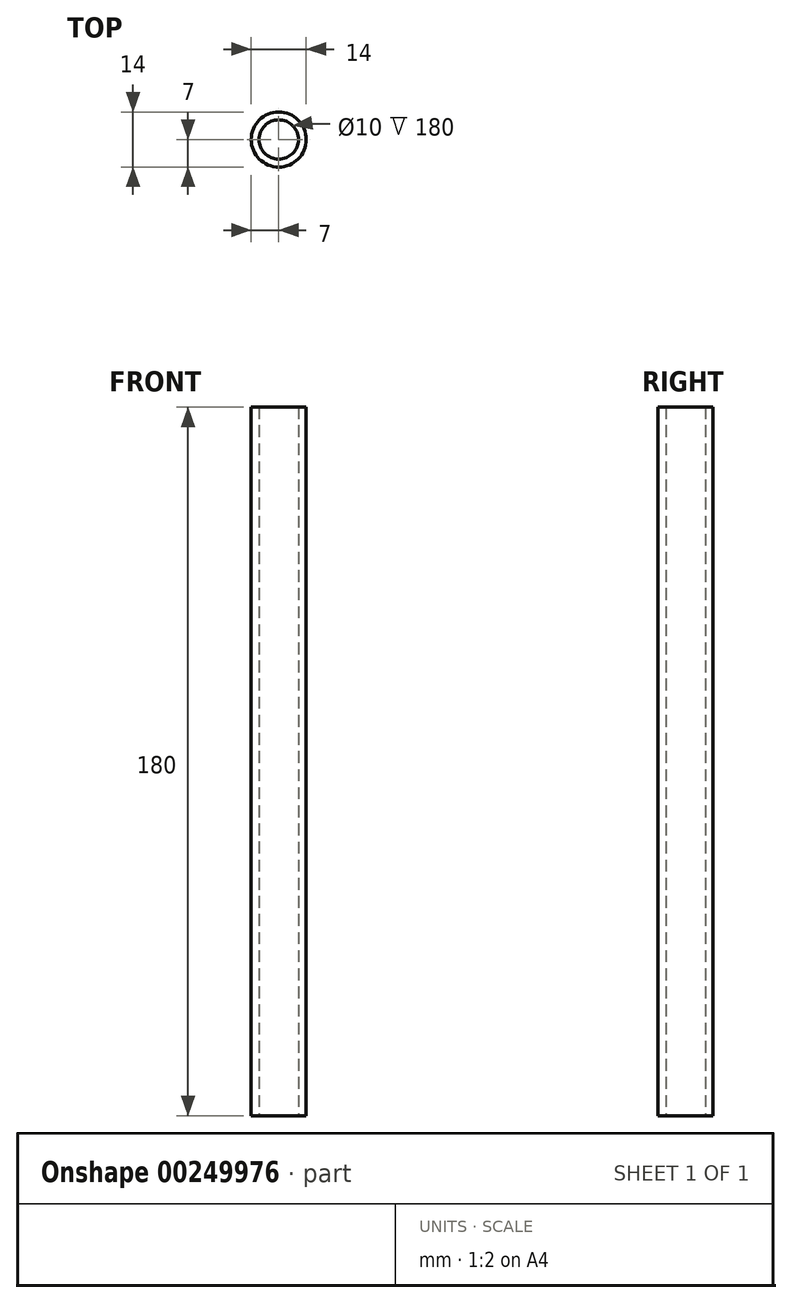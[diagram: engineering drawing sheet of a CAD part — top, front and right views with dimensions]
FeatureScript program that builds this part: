
annotation { "Feature Type Name" : "Feature", "Feature Type Description" : "" }
export const myFeature = defineFeature(function(context is Context, id is Id, definition is map)
    precondition{}
    {
        {
            var Q0;
            Q0=qCreatedBy(makeId("Top.planeOp"),FACE);
            var sketch = newSketch(context, id + "F0", { "sketchPlane" : qUnion([Q0])});
            skCircle(sketch, "E0", {"center": v(0, 0) * mm, "radius": 5 * mm});
            skCircle(sketch, "E1", {"center": v(0, 0) * mm, "radius": 7 * mm});
            skSolve(sketch);
        }
        {
            var Q0;
            Q0=qSketchRegion(id+"F0",true);
            extrude(context, id + "F1", {"entities" : qUnion([Q0]), "depth" : 180 * mm});
        }
    });
